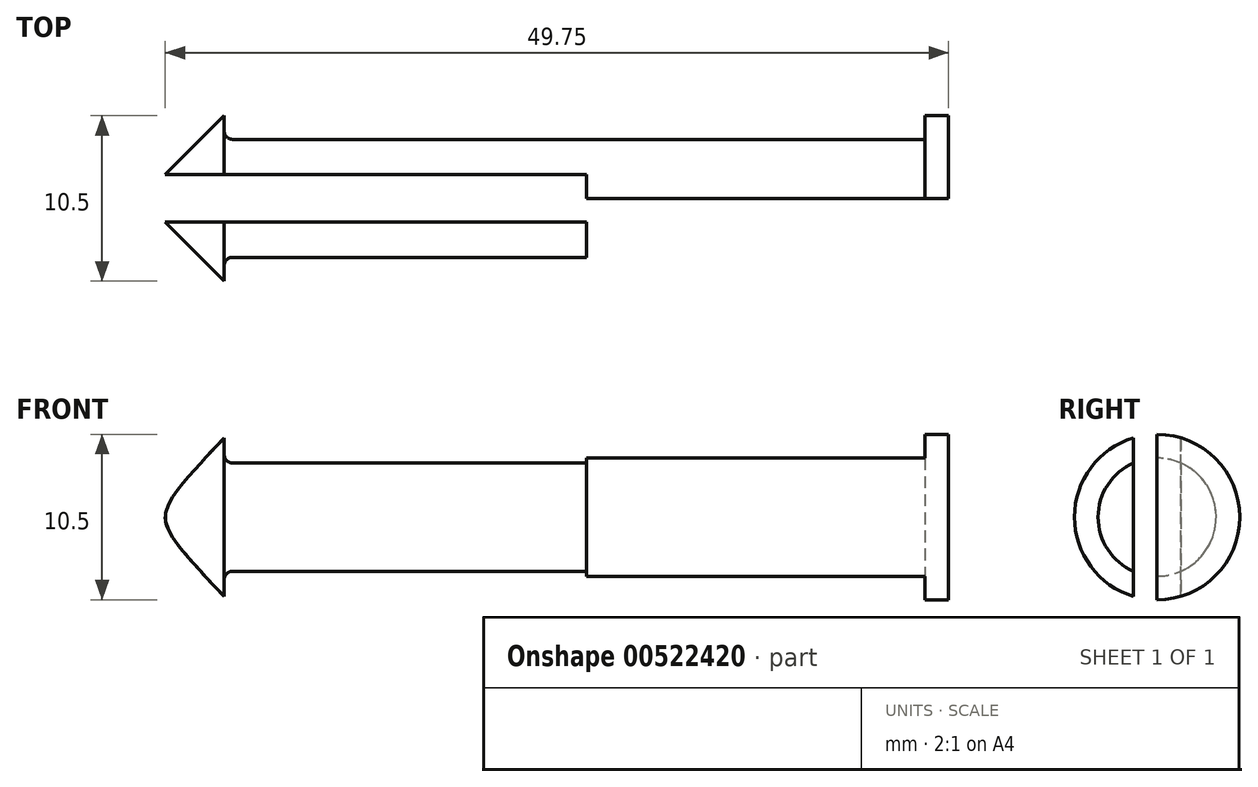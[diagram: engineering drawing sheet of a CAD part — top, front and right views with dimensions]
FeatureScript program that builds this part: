
annotation { "Feature Type Name" : "Feature", "Feature Type Description" : "" }
export const myFeature = defineFeature(function(context is Context, id is Id, definition is map)
    precondition{}
    {
        {
            var Q0;
            Q0=qCreatedBy(makeId("Top.planeOp"),FACE);
            var sketch = newSketch(context, id + "F0", { "sketchPlane" : qUnion([Q0])});
            skLineSegment(sketch, "E0.bottom", {"start": v(21.5, 3.75) * mm, "end": v(11.5, 3.75) * mm});
            skLineSegment(sketch, "E0.top", {"start": v(21.5, -3.75) * mm, "end": v(-23, -3.75) * mm});
            skLineSegment(sketch, "E0.left", {"start": v(23, 3.75) * mm, "end": v(23, 1.5) * mm});
            skPoint(sketch, "E0.middle", {"position": v(0, 0) * mm});
            skLineSegment(sketch, "E1", {"start": v(0, 3.75) * mm, "end": v(-23, 3.75) * mm});
            skLineSegment(sketch, "E2", {"start": v(11.5, 3.75) * mm, "end": v(0, 3.75) * mm});
            skLineSegment(sketch, "E3.trimOffspring", {"start": v(23, -1.5) * mm, "end": v(23, -3.75) * mm});
            skLineSegment(sketch, "E4.MirrorCS", {"start": v(-11.5, -1.5) * mm, "end": v(-23, -1.5) * mm});
            skLineSegment(sketch, "E5.MirrorCS", {"start": v(-11.5, 1.5) * mm, "end": v(-23, 1.5) * mm});
            skLineSegment(sketch, "E6", {"start": v(-23, 3.75) * mm, "end": v(-23, 5.25) * mm});
            skLineSegment(sketch, "E7", {"start": v(-23, 1.5) * mm, "end": v(-26.75, 1.5) * mm});
            skLineSegment(sketch, "E8", {"start": v(-23, 5.25) * mm, "end": v(-26.75, 1.5) * mm});
            skLineSegment(sketch, "E9.MirrorCS", {"start": v(-23, -1.5) * mm, "end": v(-26.75, -1.5) * mm});
            skLineSegment(sketch, "E10.MirrorCS", {"start": v(-23, -5.25) * mm, "end": v(-26.75, -1.5) * mm});
            skLineSegment(sketch, "E11.MirrorCS", {"start": v(-23, -3.75) * mm, "end": v(-23, -5.25) * mm});
            skLineSegment(sketch, "E12", {"start": v(23, 3.75) * mm, "end": v(23, -3.75) * mm});
            skLineSegment(sketch, "E13", {"start": v(0, 0) * mm, "end": v(23, 0) * mm});
            skLineSegment(sketch, "E14", {"start": v(-26.75, 1.5) * mm, "end": v(-26.75, -1.5) * mm});
            skLineSegment(sketch, "E15.bottom", {"start": v(23, -3.75) * mm, "end": v(23, -3.75) * mm});
            skLineSegment(sketch, "E15.top", {"start": v(23, -5.25) * mm, "end": v(23, -5.25) * mm});
            skLineSegment(sketch, "E15.left", {"start": v(23, -3.75) * mm, "end": v(23, -5.25) * mm});
            skLineSegment(sketch, "E15.right", {"start": v(23, -3.75) * mm, "end": v(23, -5.25) * mm});
            skLineSegment(sketch, "E16.bottom", {"start": v(23, -5.25) * mm, "end": v(21.5, -5.25) * mm});
            skLineSegment(sketch, "E16.top", {"start": v(23, 5.25) * mm, "end": v(21.5, 5.25) * mm});
            skLineSegment(sketch, "E16.left", {"start": v(23, -5.25) * mm, "end": v(23, 5.25) * mm});
            skLineSegment(sketch, "E16.right", {"start": v(21.5, -5.25) * mm, "end": v(21.5, -3.75) * mm});
            skLineSegment(sketch, "E17.trimOffspring", {"start": v(21.5, 3.75) * mm, "end": v(21.5, 5.25) * mm});
            skLineSegment(sketch, "E18", {"start": v(0, -3.75) * mm, "end": v(0, 3.75) * mm});
            skLineSegment(sketch, "E19.bottom", {"start": v(-11.5, -1.5) * mm, "end": v(0, -1.5) * mm});
            skLineSegment(sketch, "E19.top", {"start": v(-11.5, 1.5) * mm, "end": v(0, 1.5) * mm});
            skLineSegment(sketch, "E19.right", {"start": v(0, -1.5) * mm, "end": v(0, 1.5) * mm});
            skPoint(sketch, "E20.orphan", {"position": v(-11.5, -1.5) * mm});
            skPoint(sketch, "E21.MirrorCS.start.orphan", {"position": v(-11.5, 1.5) * mm});
            skPoint(sketch, "E22.orphan", {"position": v(-11.5, 0) * mm});
            skSolve(sketch);
        }
        {
            var Q0;
            {var subQ2=sQuery(id+"F0.wireOp",EDGE,"E0.top");Q0=makeQuery(id+"F0.imprint","IMPRINT",FACE,{"disambiguationData":[TD([[makeQuery(id+"F0.imprint","IMPRINT",EDGE,{"derivedFrom":subQ2}),-1.0]])]});}
            var Q1;
            Q1=sQuery(id+"F0.wireOp",EDGE,"E13");
            revolve(context, id + "F1", {"entities" : qUnion([Q0]), "axis" : qUnion([Q1]), "revolveType" : RevolveType.TWO_DIRECTIONS, "angle" : 90 * degree, "angleBack" : 270 * degree});
        }
        {
            var Q0;
            {var subQ1=sQuery(id+"F0.wireOp",EDGE,"E0.bottom");Q0=makeQuery(id+"F0.imprint","IMPRINT",FACE,{"disambiguationData":[TD([[makeQuery(id+"F0.imprint","IMPRINT",EDGE,{"derivedFrom":subQ1}),1.0]])]});}
            var Q1;
            {var subQ0=sQuery(id+"F0.wireOp",EDGE,"E1");Q1=makeQuery(id+"F0.imprint","IMPRINT",FACE,{"disambiguationData":[TD([[makeQuery(id+"F0.imprint","IMPRINT",EDGE,{"derivedFrom":subQ0}),1.0]])]});}
            var Q2;
            Q2=sQuery(id+"F0.wireOp",EDGE,"E13");
            revolve(context, id + "F2", {"operationType" : NewBodyOperationType.ADD, "entities" : qUnion([Q0, Q1]), "axis" : qUnion([Q2]), "revolveType" : RevolveType.TWO_DIRECTIONS, "angle" : 90 * degree, "angleBack" : 270 * degree});
        }
        {
            var Q0;
            {var subQ2=sQuery(id+"F0.wireOp",EDGE,"E4.MirrorCS");Q0=makeQuery(id+"F0.imprint","IMPRINT",FACE,{"disambiguationData":[TD([[makeQuery(id+"F0.imprint","IMPRINT",EDGE,{"derivedFrom":subQ2}),-1.0]])]});}
            extrude(context, id + "F3", {"entities" : qUnion([Q0]), "operationType" : NewBodyOperationType.REMOVE, "endBound" : BoundingType.SYMMETRIC, "depth" : 11 * mm, "offsetDistance" : 25 * mm});
        }
        {
            var Q0;
            {var subQ0=sQuery(id+"F0.wireOp",EDGE,"E1");var subQ1=sQuery(id+"F0.wireOp",EDGE,"E6");var subQ2=sQuery(id+"F0.wireOp",EDGE,"E11.MirrorCS");var subQ3=sQuery(id+"F0.wireOp",EDGE,"E0.top");Q0=makeQuery(id+"F3.boolean.opBoolean","SPLIT",EDGE,{"disambiguationData":[TD([makeQuery(id+"F3.opExtrude","SWEPT_FACE",FACE,{"disambiguationData":[OSD([sQuery(id+"F0.wireOp",EDGE,"E5.MirrorCS"),sQuery(id+"F0.wireOp",EDGE,"E7")])]})])],"derivedFrom":makeQuery(id+"F2.boolean.opBoolean","MERGE",EDGE,{"derivedFrom":[makeQuery(id+"F1.opRevolve","SWEPT_EDGE",EDGE,{"disambiguationData":[OSD([subQ3,subQ2])]}),makeQuery(id+"F2.opRevolve","SWEPT_EDGE",EDGE,{"disambiguationData":[OSD([subQ0,subQ1])]})]})});}
            var Q1;
            {var subQ0=sQuery(id+"F0.wireOp",EDGE,"E1");var subQ1=sQuery(id+"F0.wireOp",EDGE,"E6");var subQ2=sQuery(id+"F0.wireOp",EDGE,"E11.MirrorCS");var subQ3=sQuery(id+"F0.wireOp",EDGE,"E0.top");Q1=makeQuery(id+"F3.boolean.opBoolean","SPLIT",EDGE,{"disambiguationData":[TD([makeQuery(id+"F3.opExtrude","SWEPT_FACE",FACE,{"disambiguationData":[OSD([sQuery(id+"F0.wireOp",EDGE,"E4.MirrorCS"),sQuery(id+"F0.wireOp",EDGE,"E9.MirrorCS")])]})])],"derivedFrom":makeQuery(id+"F2.boolean.opBoolean","MERGE",EDGE,{"derivedFrom":[makeQuery(id+"F1.opRevolve","SWEPT_EDGE",EDGE,{"disambiguationData":[OSD([subQ3,subQ2])]}),makeQuery(id+"F2.opRevolve","SWEPT_EDGE",EDGE,{"disambiguationData":[OSD([subQ0,subQ1])]})]})});}
            fillet(context, id + "F4", {"entities" : qUnion([Q0, Q1]), "radius" : 0.5 * mm, "tangentPropagation" : true, "allowEdgeOverflow" : false});
        }
    });
